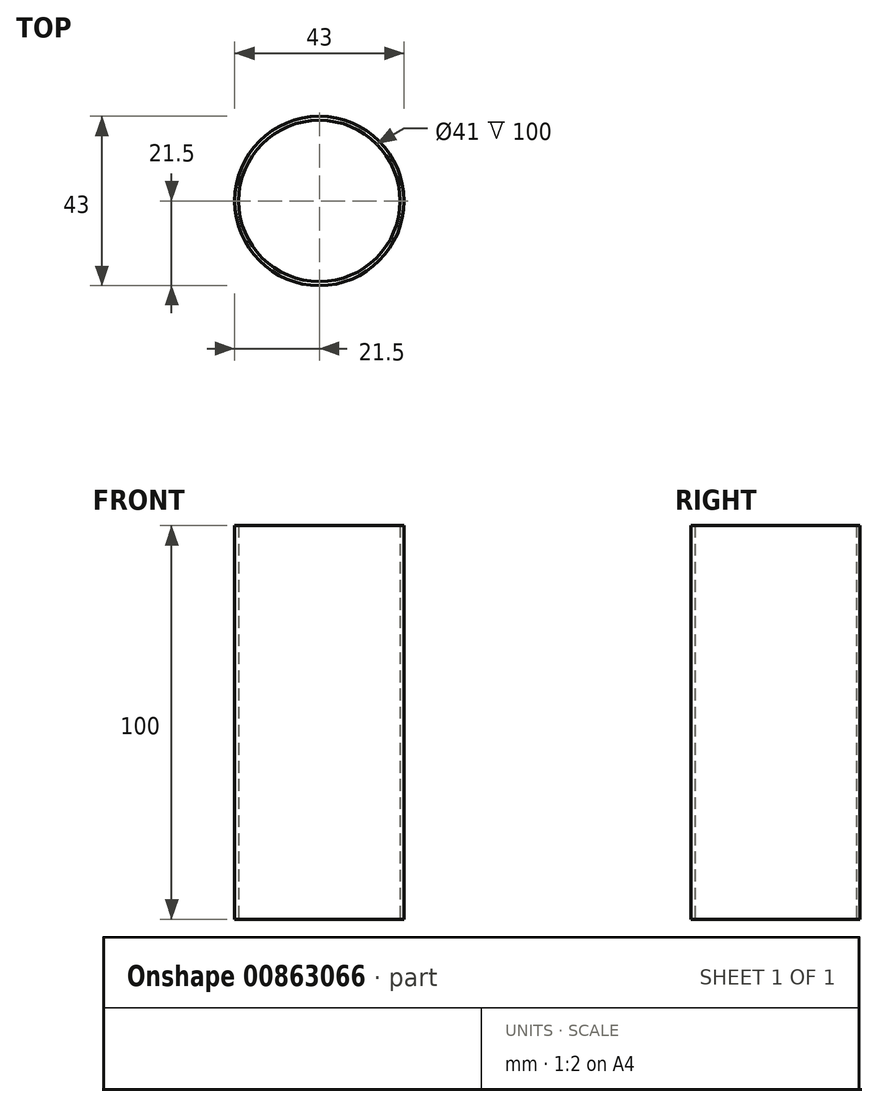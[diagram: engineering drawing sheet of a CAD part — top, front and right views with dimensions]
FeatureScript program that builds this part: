
annotation { "Feature Type Name" : "Feature", "Feature Type Description" : "" }
export const myFeature = defineFeature(function(context is Context, id is Id, definition is map)
    precondition{}
    {
        {
            var Q0;
            Q0=qCreatedBy(makeId("Top.planeOp"),FACE);
            var sketch = newSketch(context, id + "F0", { "sketchPlane" : qUnion([Q0])});
            skCircle(sketch, "E0", {"center": v(0, 0) * mm, "radius": 20.5 * mm});
            skCircle(sketch, "E1.0", {"center": v(0, 0) * mm, "radius": 21.5 * mm});
            skSolve(sketch);
        }
        {
            var Q0;
            Q0=makeQuery(id+"F0.imprint","IMPRINT",FACE,{"disambiguationData":[TD([[makeQuery(id+"F0.imprint","IMPRINT",EDGE,{"derivedFrom":sQuery(id+"F0.wireOp",EDGE,"E0")}),-1.0]])]});
            extrude(context, id + "F1", {"entities" : qUnion([Q0]), "endBound" : BoundingType.SYMMETRIC, "depth" : 100 * mm});
        }
    });
